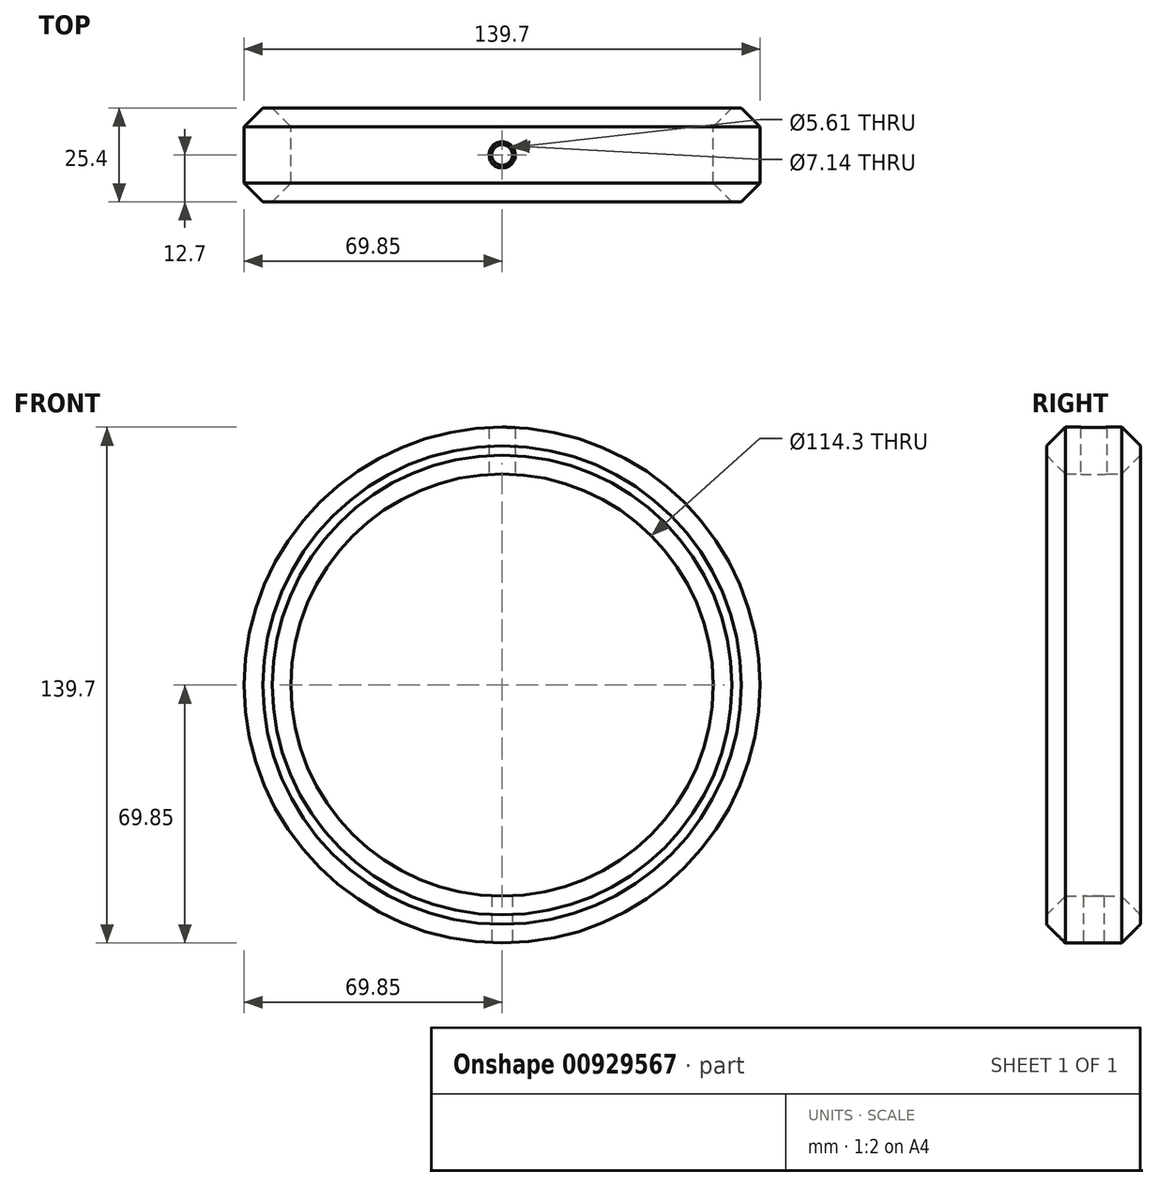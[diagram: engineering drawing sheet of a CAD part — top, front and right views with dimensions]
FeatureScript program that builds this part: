
annotation { "Feature Type Name" : "Feature", "Feature Type Description" : "" }
export const myFeature = defineFeature(function(context is Context, id is Id, definition is map)
    precondition{}
    {
        {
            var Q0;
            Q0=qCreatedBy(makeId("Front.planeOp"),FACE);
            var sketch = newSketch(context, id + "F0", { "sketchPlane" : qUnion([Q0])});
            skCircle(sketch, "E0", {"center": v(0, 0) * mm, "radius": 57.15 * mm});
            skCircle(sketch, "E1", {"center": v(0, 0) * mm, "radius": 69.85 * mm});
            skSolve(sketch);
        }
        {
            var Q0;
            Q0=makeQuery(id+"F0.imprint","IMPRINT",FACE,{"disambiguationData":[TD([[makeQuery(id+"F0.imprint","IMPRINT",EDGE,{"derivedFrom":sQuery(id+"F0.wireOp",EDGE,"E0")}),-1.0]])]});
            extrude(context, id + "F1", {"entities" : qUnion([Q0]), "depth" : 25.4 * mm, "offsetDistance" : 25.4 * mm});
        }
        {
            var Q0;
            Q0=qCreatedBy(makeId("Top.planeOp"),FACE);
            cPlane(context, id + "F2", {"entities" : qUnion([Q0]), "cplaneType" : CPlaneType.OFFSET, "offset" : 69.85 * mm, "width" : 152.4 * mm, "height" : 152.4 * mm});
        }
        {
            var Q0;
            Q0=qCreatedBy(id+"F2.planeOp",FACE);
            var sketch = newSketch(context, id + "F3", { "sketchPlane" : qUnion([Q0])});
            skLineSegment(sketch, "E2.0", {"start": v(69.85, -25.4) * mm, "end": v(-69.85, -25.4) * mm});
            skLineSegment(sketch, "E3.0", {"start": v(69.85, 0) * mm, "end": v(-69.85, 0) * mm});
            skLineSegment(sketch, "E4", {"start": v(0, 0) * mm, "end": v(0, -25.4) * mm, "construction": true});
            skPoint(sketch, "E5", {"position": v(0, -12.7) * mm});
            skSolve(sketch);
        }
        {
            var Q0;
            Q0=sQuery(id+"F3.wireOp",VERTEX,"E5");
            var Q1;
            Q1=makeQuery(id+"F1.opExtrude","SWEPT_BODY",BODY,{"disambiguationData":[OSD([sQuery(id+"F0.wireOp",EDGE,"E0"),sQuery(id+"F0.wireOp",EDGE,"E1")])]});
            hole(context, id + "F4", {"style" : HoleStyle.SIMPLE, "endStyle" : HoleEndStyle.THROUGH, "standardTappedOrClearance" : lookupTablePath({ "fit" : "Normal (ASME)", "standard" : "ANSI", "size" : "#10", "type" : "Clearance" }), "standardBlindInLast" : lookupTablePath({ "fit" : "Normal", "standard" : "ANSI", "size" : "#10", "type" : "Clearance" }), "holeDiameter" : 5.61 * mm, "majorDiameter" : 6.35 * mm, "isTappedThrough" : true, "tappedDepth" : 12.7 * mm, "tapClearance" : 3, "locations" : qUnion([Q0]), "scope" : qUnion([Q1]), "startStyle" : HoleStartStyle.PART});
        }
        {
            var Q0;
            Q0=sQuery(id+"F3.wireOp",VERTEX,"E5");
            var Q1;
            Q1=makeQuery(id+"F1.opExtrude","SWEPT_BODY",BODY,{"disambiguationData":[OSD([sQuery(id+"F0.wireOp",EDGE,"E0"),sQuery(id+"F0.wireOp",EDGE,"E1")])]});
            hole(context, id + "F5", {"style" : HoleStyle.SIMPLE, "endStyle" : HoleEndStyle.BLIND, "standardTappedOrClearance" : lookupTablePath({ "fit" : "Normal (ASME)", "standard" : "ANSI", "size" : "1/4", "type" : "Clearance" }), "standardBlindInLast" : lookupTablePath({ "fit" : "Normal", "standard" : "ANSI", "size" : "1/4", "type" : "Clearance" }), "holeDiameter" : 7.14 * mm, "majorDiameter" : 6.35 * mm, "holeDepth" : 6.35 * mm, "isTappedThrough" : true, "tappedDepth" : 12.7 * mm, "tapClearance" : 3, "locations" : qUnion([Q0]), "scope" : qUnion([Q1]), "startStyle" : HoleStartStyle.PART});
        }
        {
            var Q0;
            Q0=makeQuery(id+"F1.opExtrude","CAP_EDGE",EDGE,{"disambiguationData":[OSD([sQuery(id+"F0.wireOp",EDGE,"E1")])],"isStart":true});
            var Q1;
            Q1=makeQuery(id+"F1.opExtrude","CAP_EDGE",EDGE,{"disambiguationData":[OSD([sQuery(id+"F0.wireOp",EDGE,"E1")])],"isStart":false});
            var Q2;
            Q2=makeQuery(id+"F1.opExtrude","CAP_EDGE",EDGE,{"disambiguationData":[OSD([sQuery(id+"F0.wireOp",EDGE,"E0")])],"isStart":false});
            var Q3;
            Q3=makeQuery(id+"F1.opExtrude","CAP_EDGE",EDGE,{"disambiguationData":[OSD([sQuery(id+"F0.wireOp",EDGE,"E0")])],"isStart":true});
            chamfer(context, id + "F6", {"entities" : qUnion([Q0, Q1, Q2, Q3]), "width" : 5.08 * mm, "tangentPropagation" : true});
        }
    });
